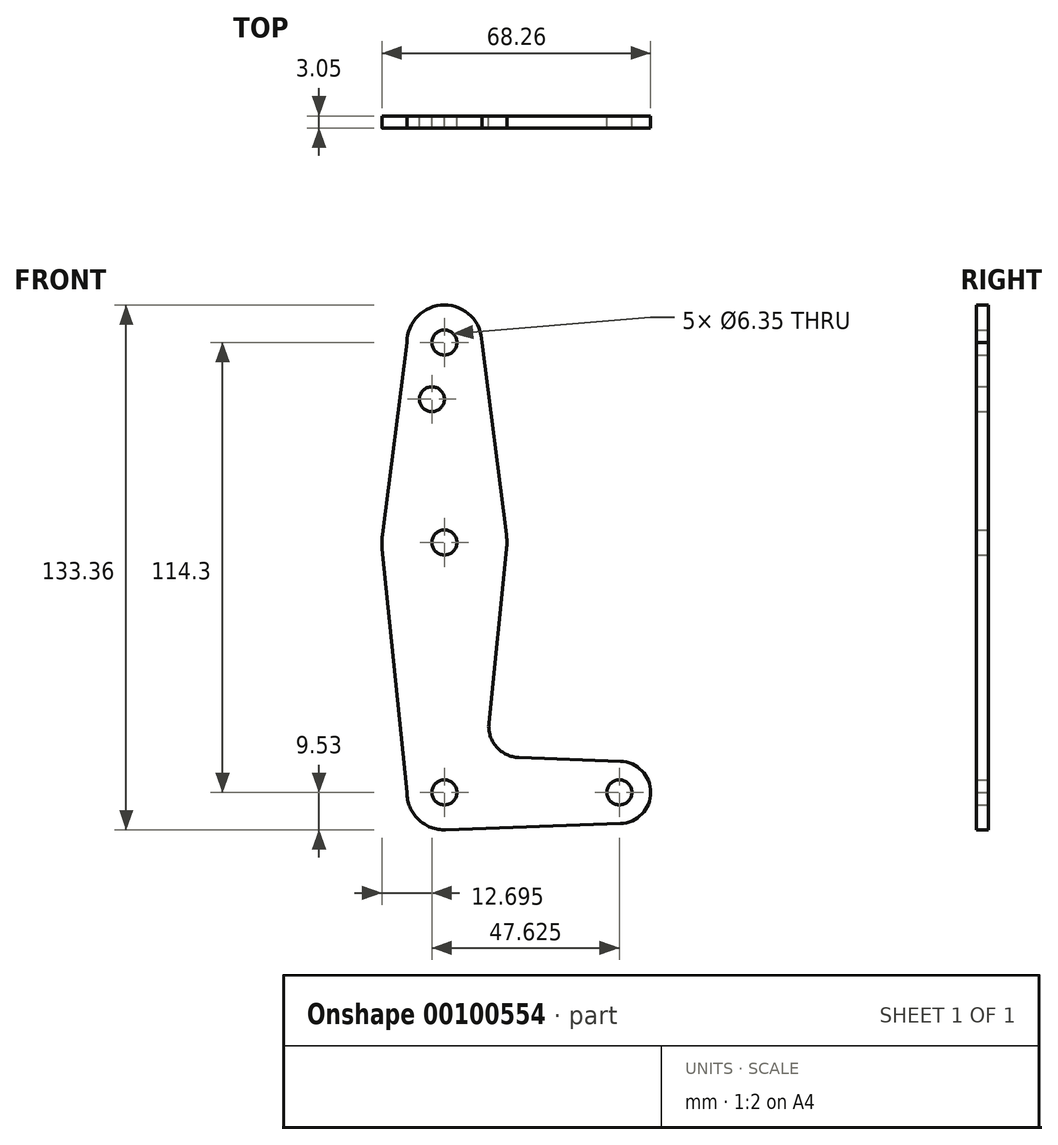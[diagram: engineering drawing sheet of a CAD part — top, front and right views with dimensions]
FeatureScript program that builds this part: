
annotation { "Feature Type Name" : "Feature", "Feature Type Description" : "" }
export const myFeature = defineFeature(function(context is Context, id is Id, definition is map)
    precondition{}
    {
        {
            var Q0;
            Q0=qCreatedBy(makeId("Front.planeOp"),FACE);
            var sketch = newSketch(context, id + "F0", { "sketchPlane" : qUnion([Q0])});
            skLineSegment(sketch, "E0", {"start": v(0, 0) * mm, "end": v(0, 114.3) * mm, "construction": true});
            skCircle(sketch, "E1", {"center": v(0, 0) * mm, "radius": 9.53 * mm});
            skCircle(sketch, "E2", {"center": v(0, 114.3) * mm, "radius": 9.53 * mm});
            skCircle(sketch, "E3", {"center": v(0, 63.5) * mm, "radius": 15.88 * mm});
            skLineSegment(sketch, "E4", {"start": v(0, 0) * mm, "end": v(44.45, 0) * mm, "construction": true});
            skCircle(sketch, "E5", {"center": v(44.45, 0) * mm, "radius": 7.94 * mm});
            skLineSegment(sketch, "E6", {"start": v(-9.52, 114.3) * mm, "end": v(-15.75, 65.5) * mm});
            skLineSegment(sketch, "E7", {"start": v(-9.52, 0) * mm, "end": v(-15.8, 61.9) * mm});
            skLineSegment(sketch, "E8", {"start": v(9.53, 114.3) * mm, "end": v(15.75, 65.5) * mm});
            skLineSegment(sketch, "E9", {"start": v(15.8, 61.9) * mm, "end": v(11.3, 17.6) * mm});
            skCircle(sketch, "E10", {"center": v(0, 114.3) * mm, "radius": 3.18 * mm});
            skCircle(sketch, "E11", {"center": v(-3.18, 99.89) * mm, "radius": 3.18 * mm});
            skCircle(sketch, "E12", {"center": v(44.45, 0) * mm, "radius": 3.18 * mm});
            skCircle(sketch, "E13", {"center": v(0, 0) * mm, "radius": 3.18 * mm});
            skCircle(sketch, "E14", {"center": v(0, 63.5) * mm, "radius": 3.18 * mm});
            skLineSegment(sketch, "E15", {"start": v(18.93, 8.85) * mm, "end": v(44.73, 7.93) * mm});
            skLineSegment(sketch, "E16", {"start": v(0.34, -9.52) * mm, "end": v(44.73, -7.93) * mm});
            skArc(sketch, "E17.filletArc", {"start": v(11.3, 17.6) * mm, "mid": v(13.22, 11.57) * mm, "end": v(18.93, 8.85) * mm});
            skSolve(sketch);
        }
        {
            var Q0;
            Q0 = qSketchRegion(id + "F0", true);
            extrude(context, id + "F1", {"entities" : qUnion([Q0]), "depth" : 3.05 * mm});
        }
    });
